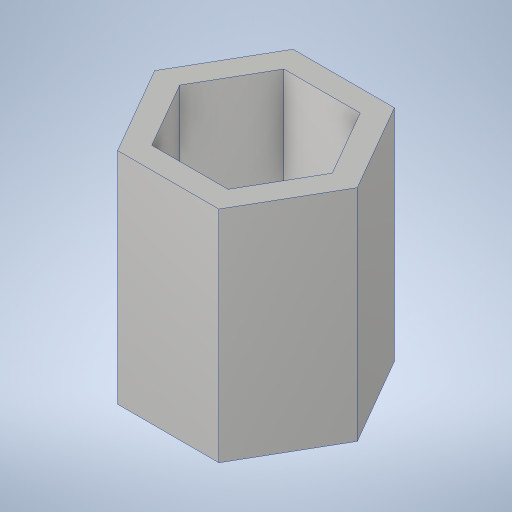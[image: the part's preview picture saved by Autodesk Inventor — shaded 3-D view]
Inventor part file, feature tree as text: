
AUTODESK INVENTOR PART (.ipt)
format: ipt  version: 2023.4 (Build 274418000, 418)  size: 219,648 bytes
history: native  units: in
note: dims shown in document units (in); Inventor stores cm internally (conversion verified against a paired STEP export)
features: extrude x1, sketch x1
ambient origin geometry x8: Origin, YZ Plane, XZ Plane, XY Plane, X Axis, Y Axis, Z Axis, Center Point
bodies: Solid1 (feature_tree)
feature tree (2):
  extrude  "Extrusion1"  Depth=0.4992in
  sketch  "Sketch1"  dims[d0=0.3758in d1=0.4992in d2=0.625in d3=0.0in]
